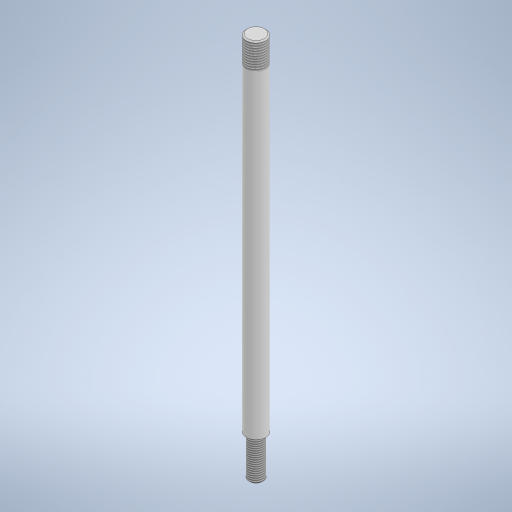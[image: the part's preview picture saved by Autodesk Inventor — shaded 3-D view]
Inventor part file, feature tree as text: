
AUTODESK INVENTOR PART (.ipt)
format: ipt  version: 2024.1 (Build 281209000, 209)  size: 253,952 bytes
history: native  units: mm
features: extrude x4, sketch x4, thread x2, chamfer x2, fillet x1
ambient origin geometry x8: Origin, YZ Plane, XZ Plane, XY Plane, X Axis, Y Axis, Z Axis, Center Point
bodies: Solid1 (feature_tree)
feature tree (13):
  extrude  "Extrusion1"  Depth=504.0mm TaperAngle=0.0deg
  extrude  "Extrusion2"  Depth=62.0mm TaperAngle=0.0deg
  fillet  "Fillet1"  Radius=2.0mm
  extrude  "Extrusion3"  Depth=12.7mm TaperAngle=0.0deg
  thread  "Thread2"  [1 undecoded]
  extrude  "Extrusion4"  Depth=2.0mm TaperAngle=0.0deg
  thread  "Thread3"  [1 undecoded]
  chamfer  "Chamfer1"  Distance=2.0mm Angle=45.0deg
  chamfer  "Chamfer2"  [1 undecoded]
  sketch  "Sketch1"  dims[d0=30.0mm d1=504.0mm d2=0.0mm]
  sketch  "Sketch2"  dims[d3=22.0mm d4=62.0mm d5=0.0mm d6=2.0mm]
  sketch  "Sketch3"  dims[d7=30.0mm d8=12.7mm d9=0.0mm d12=60.0mm d13=0.0mm]
  sketch  "Sketch4"  dims[d14=12.0mm d15=0.0mm d16=40.0mm d17=0.0mm d18=2.0mm d19=2.0mm d20=45.0deg d21=2.0mm d22=2.0mm d23=45.0deg]
note: 3 required parameter values undecoded (feature->parameter linkage not recoverable at this tier; creation-order binding heuristic only, values carry confidence <= 0.55)
